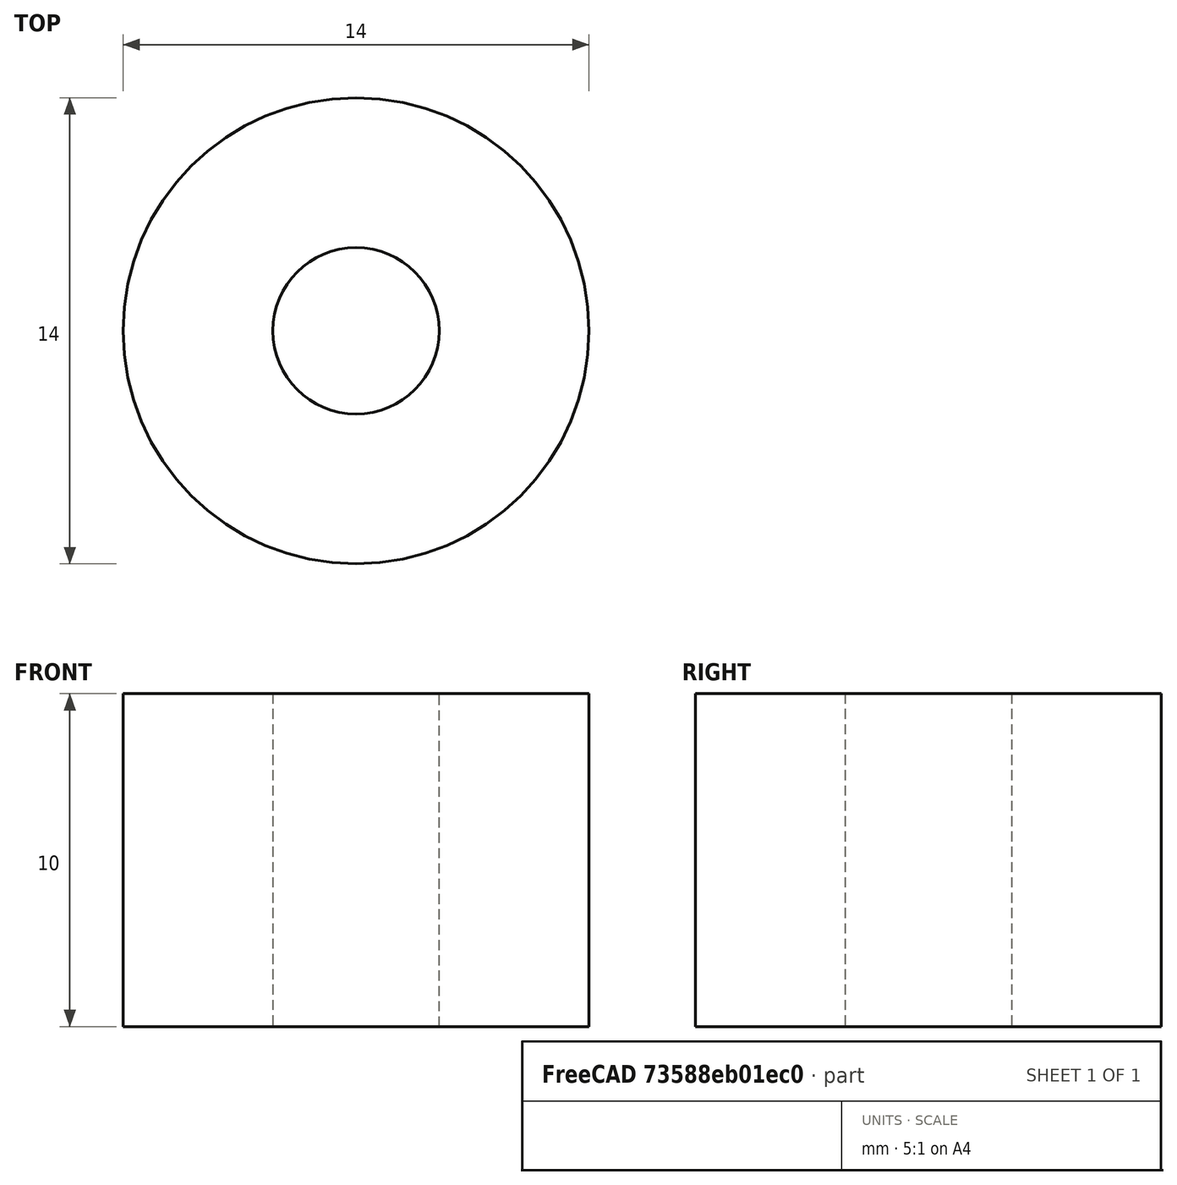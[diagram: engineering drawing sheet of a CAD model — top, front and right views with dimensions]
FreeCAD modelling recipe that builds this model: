
FCSTD DOCUMENT  (FreeCAD 0.19R24291 (Git))
Label: galetPHmettre
License: All rights reserved
LicenseURL: http://en.wikipedia.org/wiki/All_rights_reserved
objects: Sketcher::SketchObject×1, PartDesign::Pad×1, PartDesign::Body×1
note: 4 computed .brp shape members not serialized (recipe doc carries the construction recipe); baked Part::Feature solids carry a one-line shape summary decoded from their .brp

FEATURE [Sketcher::SketchObject] Sketch
  FullyConstrained = true
  MapMode = 5
  Support = -> [XY_Plane]
  sketch-geometry (2):
    g0: Circle CenterX=0 CenterY=0 CenterZ=0 NormalX=0 NormalY=0 NormalZ=1 AngleXU=0 Radius=7
    g1: Circle CenterX=0 CenterY=0 CenterZ=0 NormalX=0 NormalY=0 NormalZ=1 AngleXU=0 Radius=2.5
  constraints (4):
    c: Coincident(g0,g-1)
    c: Coincident(g1,g0)
    c: Diameter(g1) = 5
    c: Diameter(g0) = 14
FEATURE [PartDesign::Pad] Pad
  AllowMultiFace = false
  Direction = (1,1,1)
  Length = 10
  Length2 = 100
  Profile = -> Sketch
  Type = 0
FEATURE [PartDesign::Body] Body
  Group = -> [Sketch,Pad]
  Origin = -> Origin
  Tip = -> Pad
